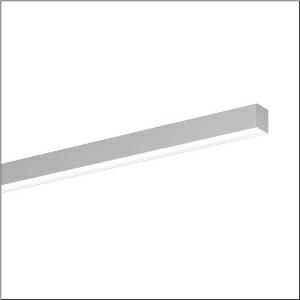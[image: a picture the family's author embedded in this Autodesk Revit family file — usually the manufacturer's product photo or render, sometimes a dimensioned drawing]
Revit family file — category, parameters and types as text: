
# Revit family: silica_r__21_51mx23dk45sb_423b
name_source: partatom
category: Lighting Fixtures
units: mm (PartAtom-declared; Revit-internal decimal feet)

## family parameters
Cut with Voids When Loaded = No
Host = Face
Light Source = No
Part Type = Normal
Room Calculation Point = No
Round Connector Dimension = Use Diameter
Shared = No

## types (1)
- --- (1 x LED, 4920 lm, 33.1 W, 4000K)
    Apparent Load = 33 VA
    CIE Flux Codes = 78 96 99 100 100
    Color Rendering = 80
    Color Temperature = 4000K
    Default Elevation = 1800 mm
    Description = Silica® 21, office luminaire, primary optical cover: prismatic diffuser, of PMMA, CAT 2 (L<= 3000cd/m²), light emission: direct distribution, primary light characteristic: symmetric, installation type: surface-mounted, LED, rated luminous flux: 4.920lm, luminous efficacy: 149lm/W, light colour: 840, colour temperature: 4000K, control gear: DALI 2, with terminal, 3+2-pole, max. 2.5mm², mains connection: 220..240V, AC, 50/60Hz, rated input power: 33.1W, luminaire housing, of aluminium, metallic grey (RAL 9006), length: 1.800mm, width: 53mm, height: 53mm, protection rating (complete): IP20, insulation class (complete): insulation class I (protective earthing), certification: CE, permissible operating ambient temperature: 0..+35°C, standard: EN 50419, packaging unit: 1 piece
    Height = 53 mm
    Lamp = 1 x LED
    Lamp Light Flux = 4920 lm
    Lamp Power = 33.1 W
    Lamp count = 1
    Length = 1804 mm
    Luminous efficacy = 149 lm/W
    Manufacturer = Siteco
    ModVariant = No
    Model = 51MX23DK45SB
    Mounting Place = Ceiling
    Mounting Type = Surface mounted
    Number of Poles = 1
    OnlyDefault = Yes
    Power Factor = 1
    Product Name = Silica® 21
    Product group = office luminaire | ceiling mounted
    ProductGroupID = 303
    Protection Class = Protection class I
    Protection Degree = IP 20
    RLX_Detail_Level = 1
    RLX_Emergency_Light_Flux = 0 lm
    RLX_Emergency_Type = 0
    RLX_Emergency_Type_DB = No
    RlxData = <blob elided: 20233 chars, md5=3c3bae69>
    Socket = socket
    Standby Power = 0 W
    System Light Flux = 4920 lm
    System Power = 33 W
    Type Comments = factory setting: luminous flux: 100 % | dim-lin: 254 | 322 mA
    Type Image = l_1335933.jpg
    URL = http://relux.com
    VarID = @adj_029523
    Voltage = 0 V
    Weight = 0.00 kg
    Width = 53 mm

## geometry (parser evidence)
native form markers: Blend x4, Sweep x11
no freeform markers — native parametric forms only
